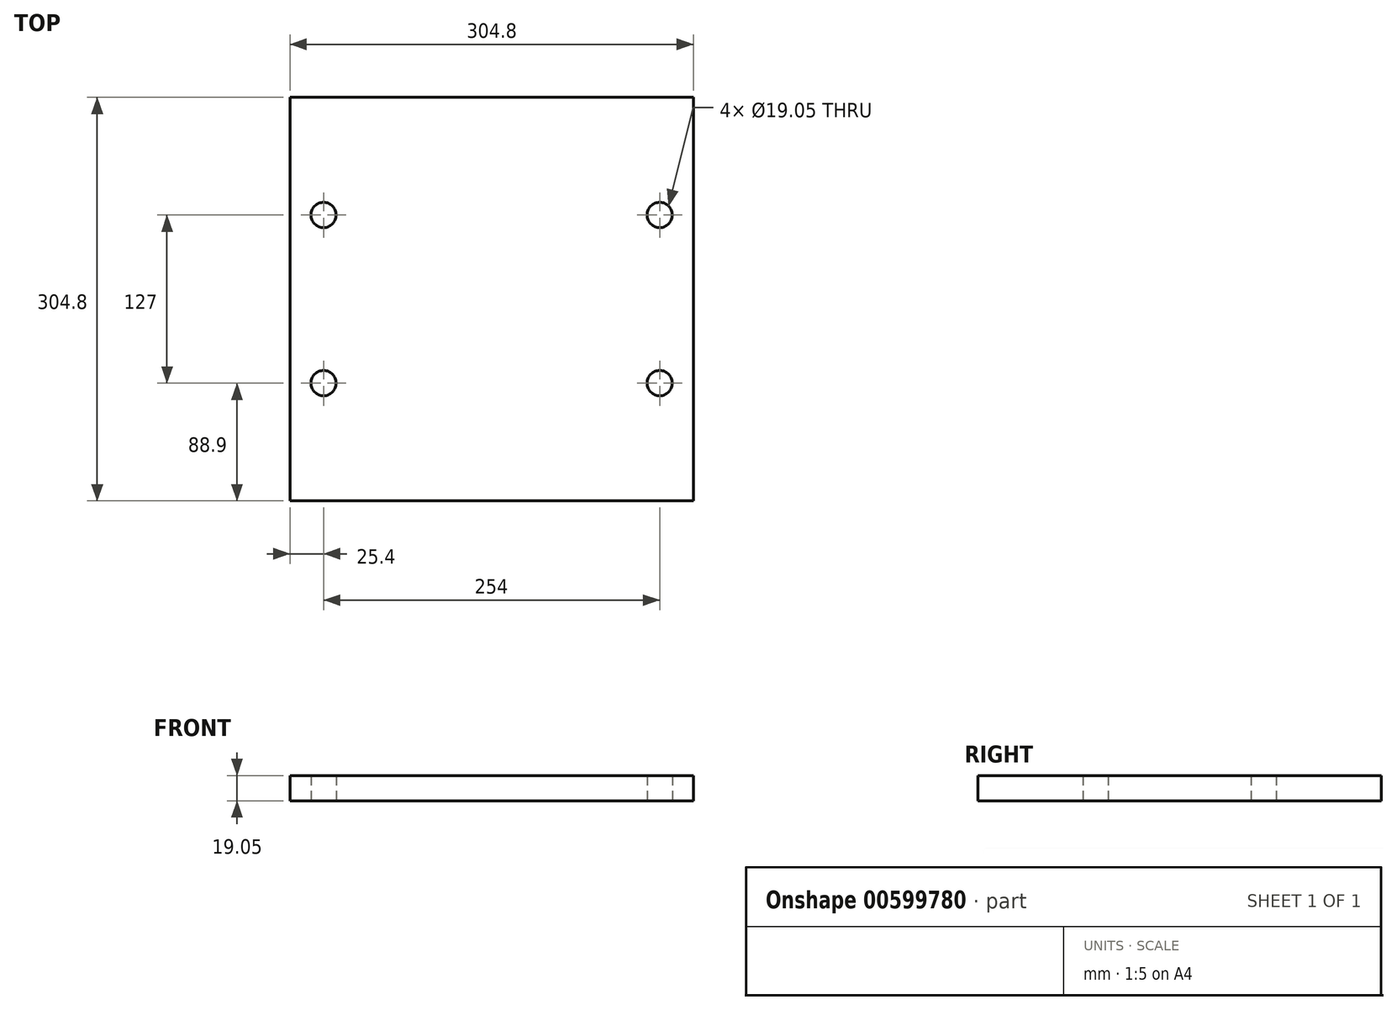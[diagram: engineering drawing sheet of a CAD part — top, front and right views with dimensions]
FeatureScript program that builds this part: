
annotation { "Feature Type Name" : "Feature", "Feature Type Description" : "" }
export const myFeature = defineFeature(function(context is Context, id is Id, definition is map)
    precondition{}
    {
        {
            var Q0;
            Q0=qCreatedBy(makeId("Top.planeOp"),FACE);
            var sketch = newSketch(context, id + "F0", { "sketchPlane" : qUnion([Q0])});
            skLineSegment(sketch, "E0.bottom", {"start": v(152.4, 152.4) * mm, "end": v(-152.4, 152.4) * mm});
            skLineSegment(sketch, "E0.top", {"start": v(152.4, -152.4) * mm, "end": v(-152.4, -152.4) * mm});
            skLineSegment(sketch, "E0.left", {"start": v(152.4, 152.4) * mm, "end": v(152.4, -152.4) * mm});
            skLineSegment(sketch, "E0.right", {"start": v(-152.4, 152.4) * mm, "end": v(-152.4, -152.4) * mm});
            skPoint(sketch, "E0.middle", {"position": v(0, 0) * mm});
            skLineSegment(sketch, "E1", {"start": v(-152.4, 0) * mm, "end": v(152.4, 0) * mm, "construction": true});
            skLineSegment(sketch, "E2", {"start": v(0, 152.4) * mm, "end": v(0, -152.4) * mm, "construction": true});
            skLineSegment(sketch, "E3", {"start": v(-127, 63.5) * mm, "end": v(-127, -63.5) * mm, "construction": true});
            skPoint(sketch, "E4", {"position": v(-127, 0) * mm});
            skCircle(sketch, "E5", {"center": v(-127, -63.5) * mm, "radius": 9.53 * mm});
            skCircle(sketch, "E6", {"center": v(-127, 63.5) * mm, "radius": 9.53 * mm});
            skCircle(sketch, "E7.MirrorC", {"center": v(127, 63.5) * mm, "radius": 9.53 * mm});
            skCircle(sketch, "E8.MirrorC", {"center": v(127, -63.5) * mm, "radius": 9.53 * mm});
            skSolve(sketch);
        }
        {
            var Q0;
            Q0 = qSketchRegion(id + "F0", true);
            extrude(context, id + "F1", {"entities" : qUnion([Q0]), "depth" : 19.05 * mm, "offsetDistance" : 25.4 * mm});
        }
    });
